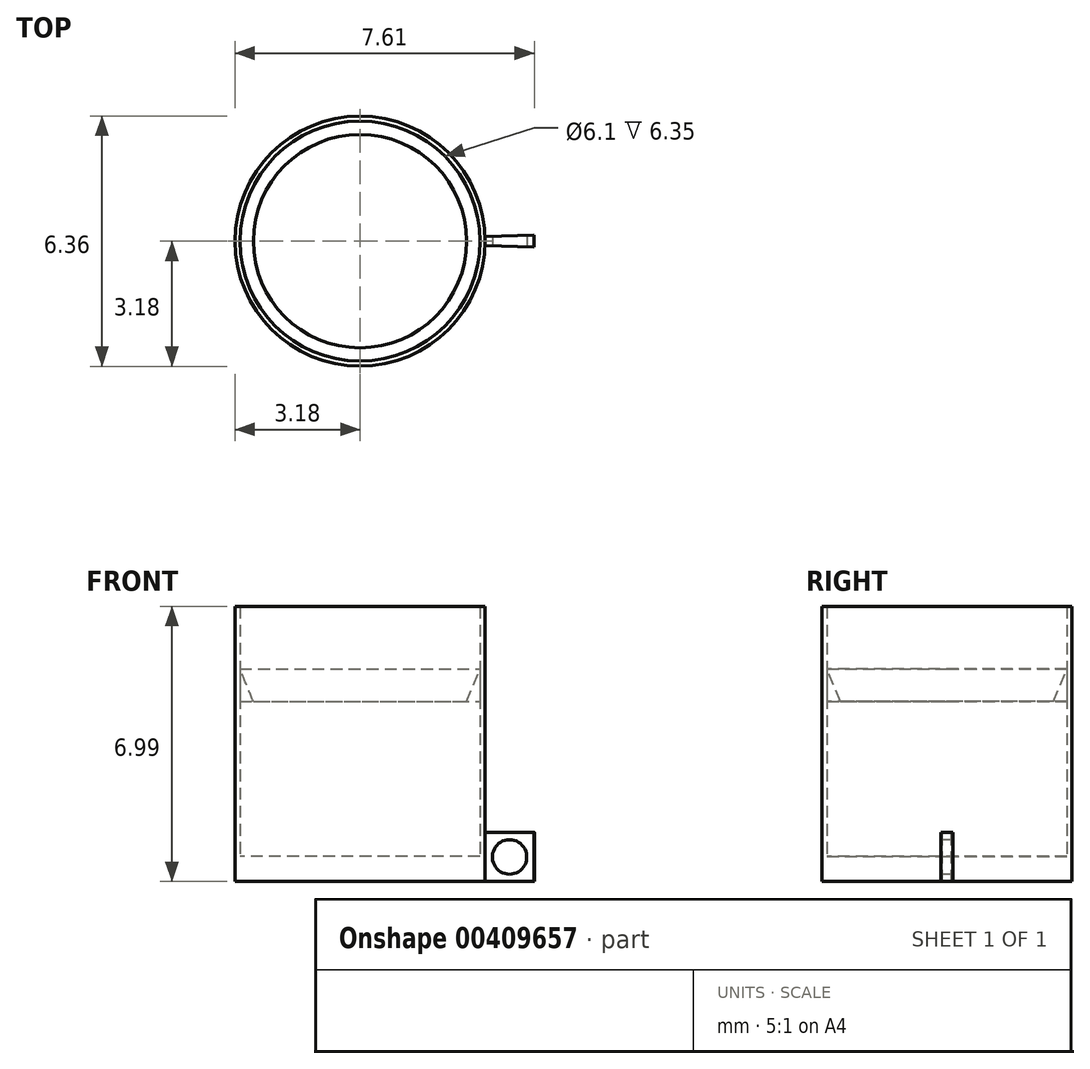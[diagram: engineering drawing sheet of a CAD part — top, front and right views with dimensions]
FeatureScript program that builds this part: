
annotation { "Feature Type Name" : "Feature", "Feature Type Description" : "" }
export const myFeature = defineFeature(function(context is Context, id is Id, definition is map)
    precondition{}
    {
        {
            var Q0;
            Q0=qCreatedBy(makeId("Top.planeOp"),FACE);
            var sketch = newSketch(context, id + "F0", { "sketchPlane" : qUnion([Q0])});
            skCircle(sketch, "E0", {"center": v(0, 0) * mm, "radius": 3.18 * mm});
            skSolve(sketch);
        }
        {
            var Q0;
            Q0 = qSketchRegion(id + "F0", true);
            extrude(context, id + "F1", {"entities" : qUnion([Q0]), "depth" : 0.64 * mm});
        }
        {
            var Q0;
            Q0=makeQuery(id+"F1.opExtrude","CAP_FACE",FACE,{"disambiguationData":[OSD([sQuery(id+"F0.wireOp",EDGE,"E0")])],"isStart":false});
            var sketch = newSketch(context, id + "F2", { "sketchPlane" : qUnion([Q0])});
            skCircle(sketch, "E1", {"center": v(0, 0) * mm, "radius": 3.18 * mm});
            skCircle(sketch, "E2", {"center": v(0, 0) * mm, "radius": 3.05 * mm});
            skSolve(sketch);
        }
        {
            var Q0;
            Q0 = qSketchRegion(id + "F2", true);
            extrude(context, id + "F3", {"entities" : qUnion([Q0]), "operationType" : NewBodyOperationType.ADD, "depth" : 6.35 * mm});
        }
        {
            var Q0;
            Q0=qCreatedBy(makeId("Front.planeOp"),FACE);
            var sketch = newSketch(context, id + "F4", { "sketchPlane" : qUnion([Q0])});
            skLineSegment(sketch, "E3", {"start": v(3.05, 5.4) * mm, "end": v(3.05, 4.57) * mm});
            skLineSegment(sketch, "E4", {"start": v(3.05, 4.57) * mm, "end": v(2.7, 4.57) * mm});
            skLineSegment(sketch, "E5", {"start": v(2.7, 4.57) * mm, "end": v(3.05, 5.4) * mm});
            skSolve(sketch);
        }
        {
            var Q0;
            Q0=qCreatedBy(makeId("Front.planeOp"),FACE);
            var sketch = newSketch(context, id + "F5", { "sketchPlane" : qUnion([Q0])});
            skLineSegment(sketch, "E6", {"start": v(0, 0) * mm, "end": v(0, 25.07) * mm, "construction": true});
            skSolve(sketch);
        }
        {
            var Q0;
            Q0 = qSketchRegion(id + "F4", true);
            var Q1;
            Q1=sQuery(id+"F5.wireOp",EDGE,"E6");
            revolve(context, id + "F6", {"entities" : qUnion([Q0]), "axis" : qUnion([Q1]), "revolveType" : RevolveType.FULL});
        }
        {
            var Q0;
            Q0=qCreatedBy(makeId("Front.planeOp"),FACE);
            var sketch = newSketch(context, id + "F7", { "sketchPlane" : qUnion([Q0])});
            skLineSegment(sketch, "E7.bottom", {"start": v(3.18, 0) * mm, "end": v(4.43, 0) * mm});
            skLineSegment(sketch, "E7.top", {"start": v(3.18, 1.25) * mm, "end": v(4.43, 1.25) * mm});
            skLineSegment(sketch, "E7.left", {"start": v(3.18, 0) * mm, "end": v(3.18, 1.25) * mm});
            skLineSegment(sketch, "E7.right", {"start": v(4.43, 0) * mm, "end": v(4.43, 1.25) * mm});
            skLineSegment(sketch, "E8", {"start": v(3.18, 1.25) * mm, "end": v(4.43, 0) * mm, "construction": true});
            skCircle(sketch, "E9", {"center": v(3.8, 0.62) * mm, "radius": 0.44 * mm});
            skSolve(sketch);
        }
        {
            var Q0;
            Q0=makeQuery(id+"F7.imprint","IMPRINT",FACE,{"disambiguationData":[TD([[makeQuery(id+"F7.imprint","IMPRINT",EDGE,{"derivedFrom":sQuery(id+"F7.wireOp",EDGE,"E7.bottom")}),1.0]])]});
            var Q1;
            Q1=sQuery(id+"F5.wireOp",EDGE,"E6");
            revolve(context, id + "F8", {"entities" : qUnion([Q0]), "axis" : qUnion([Q1]), "revolveType" : RevolveType.TWO_DIRECTIONS, "angle" : 2 * degree, "angleBack" : 358 * degree});
        }
    });
